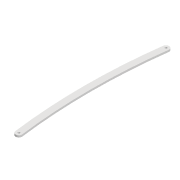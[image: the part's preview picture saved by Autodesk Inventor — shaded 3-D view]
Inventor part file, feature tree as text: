
AUTODESK INVENTOR PART (.ipt)
format: ipt  version: 2022 (Build 260153000, 153)  size: 94,720 bytes
history: native  units: mm
features: extrude x1, sketch x1
ambient origin geometry x8: Origin, YZ Plane, XZ Plane, XY Plane, X Axis, Y Axis, Z Axis, Center Point
bodies: Solid1 (feature_tree)
feature tree (2):
  extrude  "Extrusion1"  Depth=900.0mm
  sketch  "Sketch1"  dims[d0=3.3mm d1=3.3mm d2=10.0mm d3=230.652mm d6=3.0mm d7=0.0mm d14=900.0mm d15=900.0mm]
